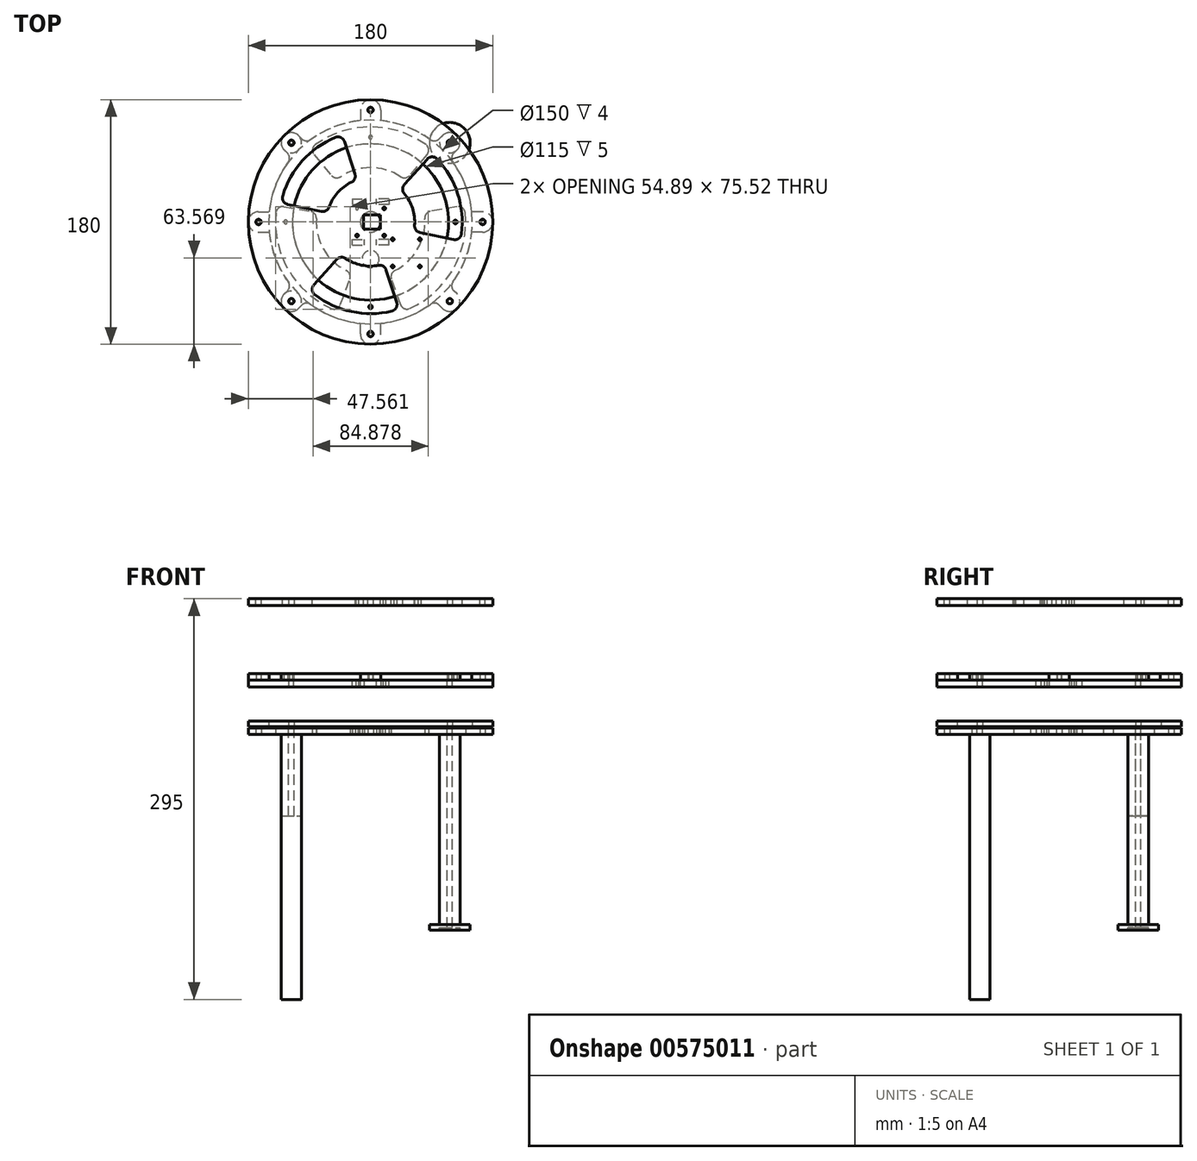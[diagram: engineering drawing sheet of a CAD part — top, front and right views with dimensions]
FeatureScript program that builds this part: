
annotation { "Feature Type Name" : "Feature", "Feature Type Description" : "" }
export const myFeature = defineFeature(function(context is Context, id is Id, definition is map)
    precondition{}
    {
        {
            var Q0;
            Q0=qCreatedBy(makeId("Top.planeOp"),FACE);
            var sketch = newSketch(context, id + "F0", { "sketchPlane" : qUnion([Q0])});
            skCircle(sketch, "E0", {"center": v(0, 0) * mm, "radius": 90 * mm});
            skCircle(sketch, "E1", {"center": v(0, 0) * mm, "radius": 75 * mm});
            skLineSegment(sketch, "E2", {"start": v(-75, 0) * mm, "end": v(-90, 0) * mm, "construction": true});
            skCircle(sketch, "E3", {"center": v(0, 0) * mm, "radius": 82.5 * mm, "construction": true});
            skPoint(sketch, "E4", {"position": v(-82.5, 0) * mm});
            skLineSegment(sketch, "E5", {"start": v(0, 0) * mm, "end": v(-58.34, 58.34) * mm, "construction": true});
            skCircle(sketch, "E6", {"center": v(-58.34, 58.34) * mm, "radius": 2 * mm});
            skCircle(sketch, "E7.MirrorC", {"center": v(58.34, 58.34) * mm, "radius": 2 * mm});
            skCircle(sketch, "E8.MirrorC", {"center": v(-58.34, -58.34) * mm, "radius": 2 * mm});
            skCircle(sketch, "E9.MirrorC", {"center": v(58.34, -58.34) * mm, "radius": 2 * mm});
            skSolve(sketch);
        }
        {
            var Q0;
            Q0 = qSketchRegion(id + "F0", true);
            extrude(context, id + "F1", {"entities" : qUnion([Q0]), "depth" : 4 * mm, "offsetDistance" : 25 * mm});
        }
        {
            var Q0;
            Q0=makeQuery(id+"F1.opExtrude","CAP_FACE",FACE,{"disambiguationData":[OSD([sQuery(id+"F0.wireOp",EDGE,"E0"),sQuery(id+"F0.wireOp",EDGE,"E1"),sQuery(id+"F0.wireOp",EDGE,"E6"),sQuery(id+"F0.wireOp",EDGE,"E7.MirrorC"),sQuery(id+"F0.wireOp",EDGE,"E8.MirrorC"),sQuery(id+"F0.wireOp",EDGE,"E9.MirrorC")])],"isStart":true});
            cPlane(context, id + "F2", {"entities" : qUnion([Q0]), "cplaneType" : CPlaneType.OFFSET, "offset" : 1 * mm, "width" : 150 * mm, "height" : 150 * mm});
        }
        {
            var Q0;
            Q0=qCreatedBy(id+"F2.planeOp",FACE);
            var sketch = newSketch(context, id + "F3", { "sketchPlane" : qUnion([Q0])});
            skCircle(sketch, "E10.0", {"center": v(0, 0) * mm, "radius": 90 * mm});
            skCircle(sketch, "E11.0", {"center": v(-58.34, 58.34) * mm, "radius": 2 * mm});
            skCircle(sketch, "E12.0", {"center": v(58.34, 58.34) * mm, "radius": 2 * mm});
            skCircle(sketch, "E13.0", {"center": v(58.34, -58.34) * mm, "radius": 2 * mm});
            skCircle(sketch, "E14.0", {"center": v(-58.34, -58.34) * mm, "radius": 2 * mm});
            skCircle(sketch, "E15", {"center": v(0, 0) * mm, "radius": 7.55 * mm});
            skSolve(sketch);
        }
        {
            var Q0;
            Q0 = qSketchRegion(id + "F3", true);
            extrude(context, id + "F4", {"entities" : qUnion([Q0]), "depth" : 5 * mm, "offsetDistance" : 25 * mm});
        }
        {
            var Q0;
            Q0=makeQuery(id+"F4.opExtrude","CAP_FACE",FACE,{"disambiguationData":[OSD([sQuery(id+"F3.wireOp",EDGE,"E10.0"),sQuery(id+"F3.wireOp",EDGE,"E11.0"),sQuery(id+"F3.wireOp",EDGE,"E12.0"),sQuery(id+"F3.wireOp",EDGE,"E13.0"),sQuery(id+"F3.wireOp",EDGE,"E14.0"),sQuery(id+"F3.wireOp",EDGE,"E15")])],"isStart":true});
            var sketch = newSketch(context, id + "F5", { "sketchPlane" : qUnion([Q0])});
            skLineSegment(sketch, "E16.bottom", {"start": v(-10, 10) * mm, "end": v(10, 10) * mm, "construction": true});
            skLineSegment(sketch, "E16.top", {"start": v(-10, -10) * mm, "end": v(10, -10) * mm, "construction": true});
            skLineSegment(sketch, "E16.left", {"start": v(-10, 10) * mm, "end": v(-10, -10) * mm, "construction": true});
            skLineSegment(sketch, "E16.right", {"start": v(10, 10) * mm, "end": v(10, -10) * mm, "construction": true});
            skPoint(sketch, "E16.middle", {"position": v(0, 0) * mm});
            skCircle(sketch, "E17", {"center": v(-10, 10) * mm, "radius": 1 * mm});
            skCircle(sketch, "E18.MirrorC", {"center": v(10, 10) * mm, "radius": 1 * mm});
            skCircle(sketch, "E19.MirrorC", {"center": v(-10, -10) * mm, "radius": 1 * mm});
            skCircle(sketch, "E20.MirrorC", {"center": v(10, -10) * mm, "radius": 1 * mm});
            skSolve(sketch);
        }
        {
            var Q0;
            Q0 = qSketchRegion(id + "F5", true);
            extrude(context, id + "F6", {"entities" : qUnion([Q0]), "operationType" : NewBodyOperationType.REMOVE, "endBound" : BoundingType.UP_TO_NEXT, "oppositeDirection" : true, "depth" : 25 * mm, "offsetDistance" : 25 * mm});
        }
        {
            var Q0;
            Q0=makeQuery(id+"F4.opExtrude","CAP_FACE",FACE,{"disambiguationData":[OSD([sQuery(id+"F3.wireOp",EDGE,"E10.0"),sQuery(id+"F3.wireOp",EDGE,"E11.0"),sQuery(id+"F3.wireOp",EDGE,"E12.0"),sQuery(id+"F3.wireOp",EDGE,"E13.0"),sQuery(id+"F3.wireOp",EDGE,"E14.0"),sQuery(id+"F3.wireOp",EDGE,"E15")])],"isStart":false});
            var sketch = newSketch(context, id + "F7", { "sketchPlane" : qUnion([Q0])});
            skPoint(sketch, "E21.center", {"position": v(0, 0) * mm});
            skCircle(sketch, "E22", {"center": v(-58.34, 58.34) * mm, "radius": 7.5 * mm});
            skSolve(sketch);
        }
        {
            var Q0;
            Q0 = qSketchRegion(id + "F7", true);
            extrude(context, id + "F8", {"entities" : qUnion([Q0]), "depth" : 195 * mm, "offsetDistance" : 25 * mm});
        }
        {
            var Q0;
            Q0=makeQuery(id+"F4.opExtrude","CAP_FACE",FACE,{"disambiguationData":[OSD([sQuery(id+"F3.wireOp",EDGE,"E10.0"),sQuery(id+"F3.wireOp",EDGE,"E11.0"),sQuery(id+"F3.wireOp",EDGE,"E12.0"),sQuery(id+"F3.wireOp",EDGE,"E13.0"),sQuery(id+"F3.wireOp",EDGE,"E14.0"),sQuery(id+"F3.wireOp",EDGE,"E15")])],"isStart":false});
            cPlane(context, id + "F9", {"entities" : qUnion([Q0]), "cplaneType" : CPlaneType.OFFSET, "offset" : 20 * mm, "oppositeDirection" : true, "width" : 150 * mm, "height" : 150 * mm});
        }
        {
            var Q0;
            Q0=makeQuery(id+"F4.opExtrude","SWEPT_BODY",BODY,{"disambiguationData":[OSD([sQuery(id+"F3.wireOp",EDGE,"E10.0"),sQuery(id+"F3.wireOp",EDGE,"E11.0"),sQuery(id+"F3.wireOp",EDGE,"E12.0"),sQuery(id+"F3.wireOp",EDGE,"E13.0"),sQuery(id+"F3.wireOp",EDGE,"E14.0"),sQuery(id+"F3.wireOp",EDGE,"E15")])]});
            var Q1;
            Q1=qCreatedBy(id+"F9.planeOp",FACE);
            mirror(context, id + "F10", {"entities" : qUnion([Q0]), "mirrorPlane" : qUnion([Q1])});
        }
        {
            var Q0;
            Q0=makeQuery(id+"F10.opPattern","COPY",FACE,{"derivedFrom":makeQuery(id+"F4.opExtrude","CAP_FACE",FACE,{"disambiguationData":[OSD([sQuery(id+"F3.wireOp",EDGE,"E10.0"),sQuery(id+"F3.wireOp",EDGE,"E11.0"),sQuery(id+"F3.wireOp",EDGE,"E12.0"),sQuery(id+"F3.wireOp",EDGE,"E13.0"),sQuery(id+"F3.wireOp",EDGE,"E14.0"),sQuery(id+"F3.wireOp",EDGE,"E15")])],"isStart":false}),"instanceName":"1"});
            var sketch = newSketch(context, id + "F11", { "sketchPlane" : qUnion([Q0])});
            skLineSegment(sketch, "E23.bottom", {"start": v(13, -13) * mm, "end": v(-13, -13) * mm, "construction": true});
            skLineSegment(sketch, "E23.top", {"start": v(13, -17) * mm, "end": v(-13, -17) * mm, "construction": true});
            skLineSegment(sketch, "E23.left", {"start": v(13, -13) * mm, "end": v(13, -17) * mm, "construction": true});
            skLineSegment(sketch, "E23.right", {"start": v(-13, -13) * mm, "end": v(-13, -17) * mm, "construction": true});
            skPoint(sketch, "E23.middle", {"position": v(0, -15) * mm});
            skLineSegment(sketch, "E24", {"start": v(5, -13) * mm, "end": v(5, -17) * mm, "construction": true});
            skLineSegment(sketch, "E25.MirrorCS", {"start": v(-5, -13) * mm, "end": v(-5, -17) * mm, "construction": true});
            skLineSegment(sketch, "E26", {"start": v(5, -13) * mm, "end": v(13, -17) * mm, "construction": true});
            skPoint(sketch, "E27", {"position": v(9, -15) * mm});
            skLineSegment(sketch, "E28.bottom", {"start": v(4.5, -13) * mm, "end": v(13.5, -13) * mm});
            skLineSegment(sketch, "E28.top", {"start": v(4.5, -17) * mm, "end": v(13.5, -17) * mm});
            skLineSegment(sketch, "E28.left", {"start": v(4.5, -13) * mm, "end": v(4.5, -17) * mm});
            skLineSegment(sketch, "E28.right", {"start": v(13.5, -13) * mm, "end": v(13.5, -17) * mm});
            skLineSegment(sketch, "E29.MirrorCS", {"start": v(-4.5, -13) * mm, "end": v(-4.5, -17) * mm});
            skLineSegment(sketch, "E30.MirrorCS", {"start": v(-4.5, -13) * mm, "end": v(-13.5, -13) * mm});
            skLineSegment(sketch, "E31.MirrorCS", {"start": v(-13.5, -13) * mm, "end": v(-13.5, -17) * mm});
            skLineSegment(sketch, "E32.MirrorCS", {"start": v(-4.5, -17) * mm, "end": v(-13.5, -17) * mm});
            skLineSegment(sketch, "E33.MirrorCS", {"start": v(-13.5, 13) * mm, "end": v(-13.5, 17) * mm});
            skLineSegment(sketch, "E34.MirrorCS", {"start": v(-4.5, 13) * mm, "end": v(-13.5, 13) * mm});
            skLineSegment(sketch, "E35.MirrorCS", {"start": v(-4.5, 13) * mm, "end": v(-4.5, 17) * mm});
            skLineSegment(sketch, "E36.MirrorCS", {"start": v(-4.5, 17) * mm, "end": v(-13.5, 17) * mm});
            skLineSegment(sketch, "E37.MirrorCS", {"start": v(4.5, 13) * mm, "end": v(4.5, 17) * mm});
            skLineSegment(sketch, "E38.MirrorCS", {"start": v(4.5, 13) * mm, "end": v(13.5, 13) * mm});
            skLineSegment(sketch, "E39.MirrorCS", {"start": v(13.5, 13) * mm, "end": v(13.5, 17) * mm});
            skLineSegment(sketch, "E40.MirrorCS", {"start": v(4.5, 17) * mm, "end": v(13.5, 17) * mm});
            skSolve(sketch);
        }
        {
            var Q0;
            Q0 = qSketchRegion(id + "F11", true);
            extrude(context, id + "F12", {"entities" : qUnion([Q0]), "operationType" : NewBodyOperationType.REMOVE, "endBound" : BoundingType.UP_TO_NEXT, "oppositeDirection" : true, "depth" : 25 * mm, "offsetDistance" : 25 * mm});
        }
        {
            var Q0;
            Q0=makeQuery(id+"F10.opPattern","COPY",FACE,{"derivedFrom":makeQuery(id+"F4.opExtrude","CAP_FACE",FACE,{"disambiguationData":[OSD([sQuery(id+"F3.wireOp",EDGE,"E10.0"),sQuery(id+"F3.wireOp",EDGE,"E11.0"),sQuery(id+"F3.wireOp",EDGE,"E12.0"),sQuery(id+"F3.wireOp",EDGE,"E13.0"),sQuery(id+"F3.wireOp",EDGE,"E14.0"),sQuery(id+"F3.wireOp",EDGE,"E15")])],"isStart":false}),"instanceName":"1"});
            var sketch = newSketch(context, id + "F13", { "sketchPlane" : qUnion([Q0])});
            skCircle(sketch, "E41", {"center": v(-58.34, 58.34) * mm, "radius": 1.85 * mm});
            skCircle(sketch, "E42.0", {"center": v(-58.34, 58.34) * mm, "radius": 2 * mm});
            skCircle(sketch, "E43.1.0", {"center": v(-58.34, -58.34) * mm, "radius": 1.85 * mm});
            skCircle(sketch, "E43.1.1", {"center": v(-58.34, -58.34) * mm, "radius": 2 * mm});
            skCircle(sketch, "E43.2.0", {"center": v(58.34, -58.34) * mm, "radius": 1.85 * mm});
            skCircle(sketch, "E43.2.1", {"center": v(58.34, -58.34) * mm, "radius": 2 * mm});
            skCircle(sketch, "E43.3.0", {"center": v(58.34, 58.34) * mm, "radius": 1.85 * mm});
            skCircle(sketch, "E43.3.1", {"center": v(58.34, 58.34) * mm, "radius": 2 * mm});
            skPoint(sketch, "E43.center", {"position": v(0, 0) * mm});
            skSolve(sketch);
        }
        {
            var Q0;
            Q0 = qSketchRegion(id + "F13", true);
            var Q1;
            Q1=makeQuery(id+"F10.opPattern","COPY",FACE,{"derivedFrom":makeQuery(id+"F4.opExtrude","CAP_FACE",FACE,{"disambiguationData":[OSD([sQuery(id+"F3.wireOp",EDGE,"E10.0"),sQuery(id+"F3.wireOp",EDGE,"E11.0"),sQuery(id+"F3.wireOp",EDGE,"E12.0"),sQuery(id+"F3.wireOp",EDGE,"E13.0"),sQuery(id+"F3.wireOp",EDGE,"E14.0"),sQuery(id+"F3.wireOp",EDGE,"E15")])],"isStart":true}),"instanceName":"1"});
            extrude(context, id + "F14", {"entities" : qUnion([Q0]), "operationType" : NewBodyOperationType.ADD, "endBound" : BoundingType.UP_TO_SURFACE, "oppositeDirection" : true, "depth" : 25 * mm, "endBoundEntityFace" : qUnion([Q1]), "offsetDistance" : 25 * mm});
        }
        {
            var Q0;
            Q0=makeQuery(id+"F14.boolean.opBoolean","MERGE",FACE,{"derivedFrom":[makeQuery(id+"F10.opPattern","COPY",FACE,{"derivedFrom":makeQuery(id+"F4.opExtrude","CAP_FACE",FACE,{"disambiguationData":[OSD([sQuery(id+"F3.wireOp",EDGE,"E10.0"),sQuery(id+"F3.wireOp",EDGE,"E11.0"),sQuery(id+"F3.wireOp",EDGE,"E12.0"),sQuery(id+"F3.wireOp",EDGE,"E13.0"),sQuery(id+"F3.wireOp",EDGE,"E14.0"),sQuery(id+"F3.wireOp",EDGE,"E15")])],"isStart":false}),"instanceName":"1"}),makeQuery(id+"F14.opExtrude","CAP_FACE",FACE,{"disambiguationData":[OSD([sQuery(id+"F13.wireOp",EDGE,"E41"),sQuery(id+"F13.wireOp",EDGE,"E42.0")])],"isStart":true}),makeQuery(id+"F14.opExtrude","CAP_FACE",FACE,{"disambiguationData":[OSD([sQuery(id+"F13.wireOp",EDGE,"E43.1.0"),sQuery(id+"F13.wireOp",EDGE,"E43.1.1")])],"isStart":true}),makeQuery(id+"F14.opExtrude","CAP_FACE",FACE,{"disambiguationData":[OSD([sQuery(id+"F13.wireOp",EDGE,"E43.2.0"),sQuery(id+"F13.wireOp",EDGE,"E43.2.1")])],"isStart":true}),makeQuery(id+"F14.opExtrude","CAP_FACE",FACE,{"disambiguationData":[OSD([sQuery(id+"F13.wireOp",EDGE,"E43.3.0"),sQuery(id+"F13.wireOp",EDGE,"E43.3.1")])],"isStart":true})]});
            var sketch = newSketch(context, id + "F15", { "sketchPlane" : qUnion([Q0])});
            skCircle(sketch, "E44.0", {"center": v(-58.34, 58.34) * mm, "radius": 1.85 * mm});
            skCircle(sketch, "E45.0", {"center": v(-58.34, -58.34) * mm, "radius": 1.85 * mm});
            skCircle(sketch, "E46.0", {"center": v(58.34, -58.34) * mm, "radius": 1.85 * mm});
            skCircle(sketch, "E47.0", {"center": v(58.34, 58.34) * mm, "radius": 1.85 * mm});
            skArc(sketch, "E48", {"start": v(63.64, 53.03) * mm, "mid": v(63.64, 63.64) * mm, "end": v(53.03, 63.64) * mm});
            skCircle(sketch, "E49", {"center": v(0, 0) * mm, "radius": 57.5 * mm});
            skArc(sketch, "E50", {"start": v(47.46, 58.07) * mm, "mid": v(0, 75) * mm, "end": v(-47.46, 58.07) * mm});
            skLineSegment(sketch, "E51", {"start": v(58.34, 58.34) * mm, "end": v(63.64, 53.03) * mm, "construction": true});
            skLineSegment(sketch, "E52", {"start": v(58.34, 58.34) * mm, "end": v(0, 0) * mm, "construction": true});
            skLineSegment(sketch, "E53", {"start": v(63.64, 53.03) * mm, "end": v(58.07, 47.46) * mm});
            skLineSegment(sketch, "E54.MirrorCS", {"start": v(53.03, 63.64) * mm, "end": v(47.46, 58.07) * mm});
            skLineSegment(sketch, "E55.MirrorCS", {"start": v(-53.03, 63.64) * mm, "end": v(-47.46, 58.07) * mm});
            skArc(sketch, "E56.MirrorCS", {"start": v(-63.64, 53.03) * mm, "mid": v(-63.64, 63.64) * mm, "end": v(-53.03, 63.64) * mm});
            skLineSegment(sketch, "E57.MirrorCS", {"start": v(-63.64, 53.03) * mm, "end": v(-58.07, 47.46) * mm});
            skLineSegment(sketch, "E58.MirrorCS", {"start": v(58.34, -58.34) * mm, "end": v(59.64, -57.03) * mm, "construction": true});
            skLineSegment(sketch, "E59.MirrorCS", {"start": v(-63.64, -53.03) * mm, "end": v(-58.07, -47.46) * mm});
            skLineSegment(sketch, "E60.MirrorCS", {"start": v(63.64, -53.03) * mm, "end": v(58.07, -47.46) * mm});
            skArc(sketch, "E61.MirrorCS", {"start": v(63.64, -53.03) * mm, "mid": v(63.64, -63.64) * mm, "end": v(53.03, -63.64) * mm});
            skLineSegment(sketch, "E62.MirrorCS", {"start": v(53.03, -63.64) * mm, "end": v(47.46, -58.07) * mm});
            skLineSegment(sketch, "E63.MirrorCS", {"start": v(-53.03, -63.64) * mm, "end": v(-47.46, -58.07) * mm});
            skArc(sketch, "E64.MirrorCS", {"start": v(-63.64, -53.03) * mm, "mid": v(-63.64, -63.64) * mm, "end": v(-53.03, -63.64) * mm});
            skArc(sketch, "E65.trimOffspring", {"start": v(-58.07, 47.46) * mm, "mid": v(-75, 0) * mm, "end": v(-58.07, -47.46) * mm});
            skArc(sketch, "E66.trimOffspring", {"start": v(-47.46, -58.07) * mm, "mid": v(0, -75) * mm, "end": v(47.46, -58.07) * mm});
            skArc(sketch, "E67.trimOffspring", {"start": v(58.07, -47.46) * mm, "mid": v(75, 0) * mm, "end": v(58.07, 47.46) * mm});
            skCircle(sketch, "E68", {"center": v(0, 62.5) * mm, "radius": 1.35 * mm});
            skCircle(sketch, "E69.1.0", {"center": v(-62.5, 0) * mm, "radius": 1.35 * mm});
            skCircle(sketch, "E69.2.0", {"center": v(0, -62.5) * mm, "radius": 1.35 * mm});
            skCircle(sketch, "E70.1.3.0", {"center": v(62.5, 0) * mm, "radius": 1.35 * mm});
            skLineSegment(sketch, "E71.1.0", {"start": v(-7.5, 82.5) * mm, "end": v(-7.5, 74.62) * mm});
            skArc(sketch, "E71.1.1", {"start": v(7.5, 82.5) * mm, "mid": v(0, 90) * mm, "end": v(-7.5, 82.5) * mm});
            skLineSegment(sketch, "E71.1.2", {"start": v(7.5, 82.5) * mm, "end": v(7.5, 74.62) * mm});
            skCircle(sketch, "E71.1.3", {"center": v(0, 82.5) * mm, "radius": 1.85 * mm});
            skArc(sketch, "E71.2.1", {"start": v(-53.03, 63.64) * mm, "mid": v(-63.64, 63.64) * mm, "end": v(-63.64, 53.03) * mm});
            skLineSegment(sketch, "E71.3.0", {"start": v(-82.5, -7.5) * mm, "end": v(-74.62, -7.5) * mm});
            skArc(sketch, "E71.3.1", {"start": v(-82.5, 7.5) * mm, "mid": v(-90, 0) * mm, "end": v(-82.5, -7.5) * mm});
            skLineSegment(sketch, "E71.3.2", {"start": v(-82.5, 7.5) * mm, "end": v(-74.62, 7.5) * mm});
            skCircle(sketch, "E71.3.3", {"center": v(-82.5, 0) * mm, "radius": 1.85 * mm});
            skLineSegment(sketch, "E71.5.0", {"start": v(7.5, -82.5) * mm, "end": v(7.5, -74.62) * mm});
            skArc(sketch, "E71.5.1", {"start": v(-7.5, -82.5) * mm, "mid": v(0, -90) * mm, "end": v(7.5, -82.5) * mm});
            skLineSegment(sketch, "E71.5.2", {"start": v(-7.5, -82.5) * mm, "end": v(-7.5, -74.62) * mm});
            skCircle(sketch, "E71.5.3", {"center": v(0, -82.5) * mm, "radius": 1.85 * mm});
            skArc(sketch, "E71.6.1", {"start": v(53.03, -63.64) * mm, "mid": v(63.64, -63.64) * mm, "end": v(63.64, -53.03) * mm});
            skLineSegment(sketch, "E71.7.0", {"start": v(82.5, 7.5) * mm, "end": v(74.62, 7.5) * mm});
            skArc(sketch, "E71.7.1", {"start": v(82.5, -7.5) * mm, "mid": v(90, 0) * mm, "end": v(82.5, 7.5) * mm});
            skLineSegment(sketch, "E71.7.2", {"start": v(82.5, -7.5) * mm, "end": v(74.62, -7.5) * mm});
            skCircle(sketch, "E71.7.3", {"center": v(82.5, 0) * mm, "radius": 1.85 * mm});
            skSolve(sketch);
        }
        {
            var Q0;
            Q0 = qSketchRegion(id + "F15", true);
            extrude(context, id + "F16", {"entities" : qUnion([Q0]), "depth" : 5 * mm, "offsetDistance" : 25 * mm});
        }
        {
            var Q0;
            Q0=makeQuery(id+"F16.opExtrude","SWEPT_EDGE",EDGE,{"disambiguationData":[OSD([sQuery(id+"F15.wireOp",EDGE,"E50"),sQuery(id+"F15.wireOp",EDGE,"E55.MirrorCS")])]});
            var Q1;
            Q1=makeQuery(id+"F16.opExtrude","SWEPT_EDGE",EDGE,{"disambiguationData":[OSD([sQuery(id+"F15.wireOp",EDGE,"E50"),sQuery(id+"F15.wireOp",EDGE,"E54.MirrorCS")])]});
            var Q2;
            Q2=makeQuery(id+"F16.opExtrude","SWEPT_EDGE",EDGE,{"disambiguationData":[OSD([sQuery(id+"F15.wireOp",EDGE,"E53"),sQuery(id+"F15.wireOp",EDGE,"E67.trimOffspring")])]});
            var Q3;
            Q3=makeQuery(id+"F16.opExtrude","SWEPT_EDGE",EDGE,{"disambiguationData":[OSD([sQuery(id+"F15.wireOp",EDGE,"E60.MirrorCS"),sQuery(id+"F15.wireOp",EDGE,"E67.trimOffspring")])]});
            var Q4;
            Q4=makeQuery(id+"F16.opExtrude","SWEPT_EDGE",EDGE,{"disambiguationData":[OSD([sQuery(id+"F15.wireOp",EDGE,"E62.MirrorCS"),sQuery(id+"F15.wireOp",EDGE,"E66.trimOffspring")])]});
            var Q5;
            Q5=makeQuery(id+"F16.opExtrude","SWEPT_EDGE",EDGE,{"disambiguationData":[OSD([sQuery(id+"F15.wireOp",EDGE,"E63.MirrorCS"),sQuery(id+"F15.wireOp",EDGE,"E66.trimOffspring")])]});
            var Q6;
            Q6=makeQuery(id+"F16.opExtrude","SWEPT_EDGE",EDGE,{"disambiguationData":[OSD([sQuery(id+"F15.wireOp",EDGE,"E59.MirrorCS"),sQuery(id+"F15.wireOp",EDGE,"E65.trimOffspring")])]});
            var Q7;
            Q7=makeQuery(id+"F16.opExtrude","SWEPT_EDGE",EDGE,{"disambiguationData":[OSD([sQuery(id+"F15.wireOp",EDGE,"E57.MirrorCS"),sQuery(id+"F15.wireOp",EDGE,"E65.trimOffspring")])]});
            fillet(context, id + "F17", {"entities" : qUnion([Q0, Q1, Q2, Q3, Q4, Q5, Q6, Q7]), "radius" : 5 * mm, "tangentPropagation" : true, "allowEdgeOverflow" : false});
        }
        {
            var Q0;
            Q0=makeQuery(id+"F4.opExtrude","CAP_FACE",FACE,{"disambiguationData":[OSD([sQuery(id+"F3.wireOp",EDGE,"E10.0"),sQuery(id+"F3.wireOp",EDGE,"E11.0"),sQuery(id+"F3.wireOp",EDGE,"E12.0"),sQuery(id+"F3.wireOp",EDGE,"E13.0"),sQuery(id+"F3.wireOp",EDGE,"E14.0"),sQuery(id+"F3.wireOp",EDGE,"E15")])],"isStart":false});
            var sketch = newSketch(context, id + "F18", { "sketchPlane" : qUnion([Q0])});
            skCircle(sketch, "E72", {"center": v(58.34, -58.34) * mm, "radius": 7.5 * mm});
            skCircle(sketch, "E73.0", {"center": v(58.34, -58.34) * mm, "radius": 2 * mm});
            skSolve(sketch);
        }
        {
            var Q0;
            Q0 = qSketchRegion(id + "F18", true);
            extrude(context, id + "F19", {"entities" : qUnion([Q0]), "depth" : 140 * mm, "offsetDistance" : 25 * mm});
        }
        {
            var Q0;
            Q0=makeQuery(id+"F19.opExtrude","CAP_FACE",FACE,{"disambiguationData":[OSD([sQuery(id+"F18.wireOp",EDGE,"E72"),sQuery(id+"F18.wireOp",EDGE,"E73.0")])],"isStart":false});
            var sketch = newSketch(context, id + "F20", { "sketchPlane" : qUnion([Q0])});
            skCircle(sketch, "E74.0", {"center": v(58.34, -58.34) * mm, "radius": 7.5 * mm});
            skCircle(sketch, "E75.0", {"center": v(58.34, -58.34) * mm, "radius": 2 * mm});
            skCircle(sketch, "E76", {"center": v(58.34, -58.34) * mm, "radius": 15 * mm});
            skSolve(sketch);
        }
        {
            var Q0;
            Q0=makeQuery(id+"F20.imprint","IMPRINT",FACE,{"disambiguationData":[TD([[makeQuery(id+"F20.imprint","IMPRINT",EDGE,{"derivedFrom":sQuery(id+"F20.wireOp",EDGE,"E74.0")}),-1.0]])]});
            extrude(context, id + "F21", {"entities" : qUnion([Q0]), "depth" : 4 * mm, "offsetDistance" : 25 * mm});
        }
        {
            var Q0;
            Q0=makeQuery(id+"F19.opExtrude","CAP_FACE",FACE,{"disambiguationData":[OSD([sQuery(id+"F18.wireOp",EDGE,"E72"),sQuery(id+"F18.wireOp",EDGE,"E73.0")])],"isStart":false});
            extrude(context, id + "F22", {"entities" : qUnion([Q0]), "operationType" : NewBodyOperationType.ADD, "depth" : 2 * mm, "offsetDistance" : 25 * mm});
        }
        {
            var Q0;
            Q0=makeQuery(id+"F14.boolean.opBoolean","MERGE",FACE,{"derivedFrom":[makeQuery(id+"F10.opPattern","COPY",FACE,{"derivedFrom":makeQuery(id+"F4.opExtrude","CAP_FACE",FACE,{"disambiguationData":[OSD([sQuery(id+"F3.wireOp",EDGE,"E10.0"),sQuery(id+"F3.wireOp",EDGE,"E11.0"),sQuery(id+"F3.wireOp",EDGE,"E12.0"),sQuery(id+"F3.wireOp",EDGE,"E13.0"),sQuery(id+"F3.wireOp",EDGE,"E14.0"),sQuery(id+"F3.wireOp",EDGE,"E15")])],"isStart":false}),"instanceName":"1"}),makeQuery(id+"F14.opExtrude","CAP_FACE",FACE,{"disambiguationData":[OSD([sQuery(id+"F13.wireOp",EDGE,"E41"),sQuery(id+"F13.wireOp",EDGE,"E42.0")])],"isStart":true}),makeQuery(id+"F14.opExtrude","CAP_FACE",FACE,{"disambiguationData":[OSD([sQuery(id+"F13.wireOp",EDGE,"E43.1.0"),sQuery(id+"F13.wireOp",EDGE,"E43.1.1")])],"isStart":true}),makeQuery(id+"F14.opExtrude","CAP_FACE",FACE,{"disambiguationData":[OSD([sQuery(id+"F13.wireOp",EDGE,"E43.2.0"),sQuery(id+"F13.wireOp",EDGE,"E43.2.1")])],"isStart":true}),makeQuery(id+"F14.opExtrude","CAP_FACE",FACE,{"disambiguationData":[OSD([sQuery(id+"F13.wireOp",EDGE,"E43.3.0"),sQuery(id+"F13.wireOp",EDGE,"E43.3.1")])],"isStart":true})]});
            cPlane(context, id + "F23", {"entities" : qUnion([Q0]), "cplaneType" : CPlaneType.OFFSET, "offset" : 10 * mm, "width" : 150 * mm, "height" : 150 * mm});
        }
        {
            var Q0;
            Q0=makeQuery(id+"F4.opExtrude","SWEPT_BODY",BODY,{"disambiguationData":[OSD([sQuery(id+"F3.wireOp",EDGE,"E10.0"),sQuery(id+"F3.wireOp",EDGE,"E11.0"),sQuery(id+"F3.wireOp",EDGE,"E12.0"),sQuery(id+"F3.wireOp",EDGE,"E13.0"),sQuery(id+"F3.wireOp",EDGE,"E14.0"),sQuery(id+"F3.wireOp",EDGE,"E15")])]});
            var Q1;
            Q1=qCreatedBy(id+"F23.planeOp",FACE);
            mirror(context, id + "F24", {"entities" : qUnion([Q0]), "mirrorPlane" : qUnion([Q1])});
        }
        {
            var Q0;
            Q0=makeQuery(id+"F24.opPattern","COPY",FACE,{"derivedFrom":makeQuery(id+"F4.opExtrude","CAP_FACE",FACE,{"disambiguationData":[OSD([sQuery(id+"F3.wireOp",EDGE,"E10.0"),sQuery(id+"F3.wireOp",EDGE,"E11.0"),sQuery(id+"F3.wireOp",EDGE,"E12.0"),sQuery(id+"F3.wireOp",EDGE,"E13.0"),sQuery(id+"F3.wireOp",EDGE,"E14.0"),sQuery(id+"F3.wireOp",EDGE,"E15")])],"isStart":false}),"instanceName":"1"});
            var sketch = newSketch(context, id + "F25", { "sketchPlane" : qUnion([Q0])});
            skCircle(sketch, "E77.0", {"center": v(-10, -10) * mm, "radius": 1 * mm});
            skCircle(sketch, "E78.0", {"center": v(-10, 10) * mm, "radius": 1 * mm});
            skCircle(sketch, "E79.0", {"center": v(10, 10) * mm, "radius": 1 * mm});
            skCircle(sketch, "E80.0", {"center": v(-58.34, 58.34) * mm, "radius": 2 * mm});
            skCircle(sketch, "E81.1.0", {"center": v(-82.5, 0) * mm, "radius": 2 * mm});
            skCircle(sketch, "E81.2.0", {"center": v(-58.34, -58.34) * mm, "radius": 2 * mm});
            skCircle(sketch, "E82.1.3.0", {"center": v(0, -82.5) * mm, "radius": 2 * mm});
            skCircle(sketch, "E82.1.4.0", {"center": v(58.34, -58.34) * mm, "radius": 2 * mm});
            skCircle(sketch, "E82.1.5.0", {"center": v(82.5, 0) * mm, "radius": 2 * mm});
            skCircle(sketch, "E82.1.6.0", {"center": v(58.34, 58.34) * mm, "radius": 2 * mm});
            skCircle(sketch, "E82.1.7.0", {"center": v(0, 82.5) * mm, "radius": 2 * mm});
            skLineSegment(sketch, "E83.bottom", {"start": v(-5.25, 5.25) * mm, "end": v(7.25, 5.25) * mm});
            skLineSegment(sketch, "E83.top", {"start": v(-5.25, -5.25) * mm, "end": v(7.25, -5.25) * mm});
            skLineSegment(sketch, "E83.left", {"start": v(-5.25, 5.25) * mm, "end": v(-5.25, -5.25) * mm});
            skLineSegment(sketch, "E83.right", {"start": v(7.25, 5.25) * mm, "end": v(7.25, -5.25) * mm});
            skPoint(sketch, "E83.middle", {"position": v(1, 0) * mm});
            skLineSegment(sketch, "E84.bottom", {"start": v(16.3, -12.75) * mm, "end": v(36.3, -12.75) * mm, "construction": true});
            skLineSegment(sketch, "E84.top", {"start": v(16.3, -32.75) * mm, "end": v(36.3, -32.75) * mm, "construction": true});
            skLineSegment(sketch, "E84.left", {"start": v(16.3, -12.75) * mm, "end": v(16.3, -32.75) * mm, "construction": true});
            skLineSegment(sketch, "E84.right", {"start": v(36.3, -12.75) * mm, "end": v(36.3, -32.75) * mm, "construction": true});
            skPoint(sketch, "E84.middle", {"position": v(26.3, -22.75) * mm});
            skCircle(sketch, "E85.0", {"center": v(10, -10) * mm, "radius": 1 * mm, "construction": true});
            skCircle(sketch, "E86", {"center": v(16.3, -12.75) * mm, "radius": 1 * mm});
            skCircle(sketch, "E87.1.0", {"center": v(16.3, -32.75) * mm, "radius": 1 * mm});
            skCircle(sketch, "E87.2.0", {"center": v(36.3, -32.75) * mm, "radius": 1 * mm});
            skCircle(sketch, "E88.1.3.0", {"center": v(36.3, -12.75) * mm, "radius": 1 * mm});
            skSolve(sketch);
        }
        {
            var Q0;
            {var subQ0=sQuery(id+"F25.wireOp",EDGE,"QSQis5DJ-ndRP-tXz9-sWgT-VjHo9YrmBDyp.right");var subQ1=sQuery(id+"F25.wireOp",EDGE,"15366a01-08b8-4944-8cce-0e4f2887150d.0");var subQ2=makeQuery(id+"F25.imprint","INTERSECT",VERTEX,{"disambiguationData":[OD(0.0)],"derivedFrom":[subQ1,subQ0]});Q0=makeQuery(id+"F25.imprint","IMPRINT",FACE,{"disambiguationData":[TD([[makeQuery(id+"F25.imprint","IMPRINT",EDGE,{"disambiguationData":[TD([[subQ2,1.0]])],"derivedFrom":subQ1}),-1.0]])]});}
            var Q1;
            Q1=makeQuery(id+"F25.imprint","IMPRINT",FACE,{"disambiguationData":[TD([[makeQuery(id+"F25.imprint","IMPRINT",EDGE,{"derivedFrom":sQuery(id+"F25.wireOp",EDGE,"E78.0")}),1.0]])]});
            var Q2;
            Q2=makeQuery(id+"F25.imprint","IMPRINT",FACE,{"disambiguationData":[TD([[makeQuery(id+"F25.imprint","IMPRINT",EDGE,{"derivedFrom":sQuery(id+"F25.wireOp",EDGE,"E79.0")}),-1.0]])]});
            var Q3;
            Q3=makeQuery(id+"F25.imprint","IMPRINT",FACE,{"disambiguationData":[TD([[makeQuery(id+"F25.imprint","IMPRINT",EDGE,{"derivedFrom":sQuery(id+"F25.wireOp",EDGE,"950ba534-4a06-4b06-9c65-52ff77a1f382.0")}),1.0]])]});
            var Q4;
            Q4=makeQuery(id+"F25.imprint","IMPRINT",FACE,{"disambiguationData":[TD([[makeQuery(id+"F25.imprint","IMPRINT",EDGE,{"derivedFrom":sQuery(id+"F25.wireOp",EDGE,"E77.0")}),-1.0]])]});
            var Q5;
            {var subQ0=sQuery(id+"F25.wireOp",EDGE,"QSQis5DJ-ndRP-tXz9-sWgT-VjHo9YrmBDyp.left");var subQ1=sQuery(id+"F25.wireOp",EDGE,"15366a01-08b8-4944-8cce-0e4f2887150d.0");var subQ2=makeQuery(id+"F25.imprint","INTERSECT",VERTEX,{"disambiguationData":[OD(0.0)],"derivedFrom":[subQ1,subQ0]});Q5=makeQuery(id+"F25.imprint","IMPRINT",FACE,{"disambiguationData":[TD([[makeQuery(id+"F25.imprint","IMPRINT",EDGE,{"disambiguationData":[TD([[subQ2,-1.0]])],"derivedFrom":subQ1}),-1.0]])]});}
            var Q6;
            {var subQ0=sQuery(id+"F25.wireOp",EDGE,"QSQis5DJ-ndRP-tXz9-sWgT-VjHo9YrmBDyp.bottom");var subQ1=sQuery(id+"F25.wireOp",EDGE,"15366a01-08b8-4944-8cce-0e4f2887150d.0");var subQ2=makeQuery(id+"F25.imprint","INTERSECT",VERTEX,{"disambiguationData":[OD(0.0)],"derivedFrom":[subQ1,subQ0]});Q6=makeQuery(id+"F25.imprint","IMPRINT",FACE,{"disambiguationData":[TD([[makeQuery(id+"F25.imprint","IMPRINT",EDGE,{"disambiguationData":[TD([[subQ2,-1.0]])],"derivedFrom":subQ1}),-1.0]])]});}
            var Q7;
            {var subQ0=sQuery(id+"F25.wireOp",EDGE,"QSQis5DJ-ndRP-tXz9-sWgT-VjHo9YrmBDyp.top");var subQ1=sQuery(id+"F25.wireOp",EDGE,"15366a01-08b8-4944-8cce-0e4f2887150d.0");var subQ2=makeQuery(id+"F25.imprint","INTERSECT",VERTEX,{"disambiguationData":[OD(0.0)],"derivedFrom":[subQ1,subQ0]});Q7=makeQuery(id+"F25.imprint","IMPRINT",FACE,{"disambiguationData":[TD([[makeQuery(id+"F25.imprint","IMPRINT",EDGE,{"disambiguationData":[TD([[subQ2,-1.0]])],"derivedFrom":subQ1}),-1.0]])]});}
            var Q8;
            {var subQ0=sQuery(id+"F25.wireOp",EDGE,"E83.left");Q8=makeQuery(id+"F25.imprint","IMPRINT",FACE,{"disambiguationData":[TD([[makeQuery(id+"F25.imprint","IMPRINT",EDGE,{"derivedFrom":subQ0}),-1.0]])]});}
            var Q9;
            {var subQ0=sQuery(id+"F25.wireOp",EDGE,"E83.right");var subQ1=makeQuery(id+"F24.opPattern","COPY",EDGE,{"derivedFrom":makeQuery(id+"F4.opExtrude","CAP_EDGE",EDGE,{"disambiguationData":[OSD([sQuery(id+"F3.wireOp",EDGE,"E15")])],"isStart":false}),"instanceName":"1"});var subQ2=makeQuery(id+"F25.imprint","INTERSECT",VERTEX,{"disambiguationData":[OD(0.0)],"derivedFrom":[subQ1,subQ0]});Q9=makeQuery(id+"F25.imprint","IMPRINT",FACE,{"disambiguationData":[TD([[makeQuery(id+"F25.imprint","IMPRINT",EDGE,{"disambiguationData":[TD([[subQ2,-1.0]])],"derivedFrom":subQ0}),1.0]])]});}
            var Q10;
            {var subQ3=sQuery(id+"F25.wireOp",EDGE,"X5iIHsC0-m7Zg-54nE-1Jfu-dFlnVcUJdtpu");var subQ8=sQuery(id+"F25.wireOp",EDGE,"a78230fa-ddc7-4092-8a09-10e84057542a0.MirrorCS");var subQ9=makeQuery(id+"F25.imprint","INTERSECT",VERTEX,{"derivedFrom":[subQ3,subQ8]});Q10=makeQuery(id+"F25.imprint","IMPRINT",FACE,{"disambiguationData":[TD([[makeQuery(id+"F25.imprint","IMPRINT",EDGE,{"disambiguationData":[TD([[subQ9,1.0]])],"derivedFrom":subQ3}),1.0]])]});}
            var Q11;
            Q11=makeQuery(id+"F25.imprint","IMPRINT",FACE,{"disambiguationData":[TD([[makeQuery(id+"F25.imprint","IMPRINT",EDGE,{"derivedFrom":makeQuery(id+"F24.opPattern","COPY",EDGE,{"derivedFrom":makeQuery(id+"F6.boolean.opBoolean","COPY",EDGE,{"derivedFrom":makeQuery(id+"F6.opExtrude","TWEAK_EDGE",EDGE,{"derivedFrom":[makeQuery(id+"F4.opExtrude","CAP_FACE",FACE,{"disambiguationData":[OSD([sQuery(id+"F3.wireOp",EDGE,"E10.0"),sQuery(id+"F3.wireOp",EDGE,"E11.0"),sQuery(id+"F3.wireOp",EDGE,"E12.0"),sQuery(id+"F3.wireOp",EDGE,"E13.0"),sQuery(id+"F3.wireOp",EDGE,"E14.0"),sQuery(id+"F3.wireOp",EDGE,"E15")])],"isStart":false}),makeQuery(id+"F5.imprint","IMPRINT",EDGE,{"derivedFrom":sQuery(id+"F5.wireOp",EDGE,"E20.MirrorC")})]})}),"instanceName":"1"})}),1.0]])]});
            extrude(context, id + "F26", {"entities" : qUnion([Q0, Q1, Q2, Q3, Q4, Q5, Q6, Q7, Q8, Q9, Q10, Q11]), "operationType" : NewBodyOperationType.ADD, "oppositeDirection" : true, "depth" : 5 * mm, "offsetDistance" : 25 * mm});
        }
        {
            var Q0;
            {var subQ5=sQuery(id+"F25.wireOp",EDGE,"656fdb2e-e72c-4114-8cef-4688475ef528.filletArc");Q0=makeQuery(id+"F25.imprint","IMPRINT",FACE,{"disambiguationData":[TD([[makeQuery(id+"F25.imprint","IMPRINT",EDGE,{"derivedFrom":subQ5}),1.0]])]});}
            var Q1;
            {var subQ5=sQuery(id+"F25.wireOp",EDGE,"dae69112-de24-48df-9be6-64b79decc6ef.filletArc");Q1=makeQuery(id+"F25.imprint","IMPRINT",FACE,{"disambiguationData":[TD([[makeQuery(id+"F25.imprint","IMPRINT",EDGE,{"derivedFrom":subQ5}),1.0]])]});}
            var Q2;
            {var subQ5=sQuery(id+"F25.wireOp",EDGE,"470e9d0d-4a14-41c7-af53-fb42cd5c9400.filletArc");Q2=makeQuery(id+"F25.imprint","IMPRINT",FACE,{"disambiguationData":[TD([[makeQuery(id+"F25.imprint","IMPRINT",EDGE,{"derivedFrom":subQ5}),1.0]])]});}
            var Q3;
            {var subQ5=sQuery(id+"F25.wireOp",EDGE,"ee6f9c0c-4a7c-40b4-91d3-26762448eaf5.filletArc");Q3=makeQuery(id+"F25.imprint","IMPRINT",FACE,{"disambiguationData":[TD([[makeQuery(id+"F25.imprint","IMPRINT",EDGE,{"derivedFrom":subQ5}),1.0]])]});}
            var Q4;
            Q4=makeQuery(id+"F25.imprint","IMPRINT",FACE,{"disambiguationData":[TD([[makeQuery(id+"F25.imprint","IMPRINT",EDGE,{"derivedFrom":sQuery(id+"F25.wireOp",EDGE,"X5iIHsC0-m7Zg-54nE-1Jfu-dFlnVcUJdtpu")}),1.0]])]});
            var Q5;
            Q5=makeQuery(id+"F25.imprint","IMPRINT",FACE,{"disambiguationData":[TD([[makeQuery(id+"F25.imprint","IMPRINT",EDGE,{"derivedFrom":sQuery(id+"F25.wireOp",EDGE,"QmYIbrE2-BVum-i9cv-bLCY-xA6qm9N7vCon")}),1.0]])]});
            var Q6;
            Q6=makeQuery(id+"F25.imprint","IMPRINT",FACE,{"disambiguationData":[TD([[makeQuery(id+"F25.imprint","IMPRINT",EDGE,{"derivedFrom":sQuery(id+"F25.wireOp",EDGE,"eadecacf-8e49-4b1c-866c-a8928ed26be7.1.3.0")}),1.0]])]});
            var Q7;
            Q7=makeQuery(id+"F25.imprint","IMPRINT",FACE,{"disambiguationData":[TD([[makeQuery(id+"F25.imprint","IMPRINT",EDGE,{"derivedFrom":sQuery(id+"F25.wireOp",EDGE,"7a315e59-80f9-47be-ab7b-8afd31b71271.2.0")}),1.0]])]});
            var Q8;
            Q8=makeQuery(id+"F25.imprint","IMPRINT",FACE,{"disambiguationData":[TD([[makeQuery(id+"F25.imprint","IMPRINT",EDGE,{"derivedFrom":sQuery(id+"F25.wireOp",EDGE,"7a315e59-80f9-47be-ab7b-8afd31b71271.1.0")}),1.0]])]});
            var Q9;
            {var subQ0=sQuery(id+"F25.wireOp",EDGE,"QSQis5DJ-ndRP-tXz9-sWgT-VjHo9YrmBDyp.bottom");var subQ1=sQuery(id+"F25.wireOp",EDGE,"15366a01-08b8-4944-8cce-0e4f2887150d.0");var subQ2=makeQuery(id+"F25.imprint","INTERSECT",VERTEX,{"disambiguationData":[OD(1.0)],"derivedFrom":[subQ1,subQ0]});Q9=makeQuery(id+"F25.imprint","IMPRINT",FACE,{"disambiguationData":[TD([[makeQuery(id+"F25.imprint","IMPRINT",EDGE,{"disambiguationData":[TD([[subQ2,-1.0]])],"derivedFrom":subQ1}),1.0]])]});}
            var Q10;
            {var subQ0=sQuery(id+"F25.wireOp",EDGE,"QSQis5DJ-ndRP-tXz9-sWgT-VjHo9YrmBDyp.top");var subQ1=sQuery(id+"F25.wireOp",EDGE,"15366a01-08b8-4944-8cce-0e4f2887150d.0");var subQ2=makeQuery(id+"F25.imprint","INTERSECT",VERTEX,{"disambiguationData":[OD(0.0)],"derivedFrom":[subQ1,subQ0]});Q10=makeQuery(id+"F25.imprint","IMPRINT",FACE,{"disambiguationData":[TD([[makeQuery(id+"F25.imprint","IMPRINT",EDGE,{"disambiguationData":[TD([[subQ2,1.0]])],"derivedFrom":subQ1}),1.0]])]});}
            var Q11;
            {var subQ0=sQuery(id+"F25.wireOp",EDGE,"QSQis5DJ-ndRP-tXz9-sWgT-VjHo9YrmBDyp.top");var subQ1=sQuery(id+"F25.wireOp",EDGE,"15366a01-08b8-4944-8cce-0e4f2887150d.0");var subQ2=makeQuery(id+"F25.imprint","INTERSECT",VERTEX,{"disambiguationData":[OD(1.0)],"derivedFrom":[subQ1,subQ0]});Q11=makeQuery(id+"F25.imprint","IMPRINT",FACE,{"disambiguationData":[TD([[makeQuery(id+"F25.imprint","IMPRINT",EDGE,{"disambiguationData":[TD([[subQ2,-1.0]])],"derivedFrom":subQ1}),1.0]])]});}
            var Q12;
            {var subQ0=sQuery(id+"F25.wireOp",EDGE,"QSQis5DJ-ndRP-tXz9-sWgT-VjHo9YrmBDyp.left");var subQ1=sQuery(id+"F25.wireOp",EDGE,"15366a01-08b8-4944-8cce-0e4f2887150d.0");var subQ2=makeQuery(id+"F25.imprint","INTERSECT",VERTEX,{"disambiguationData":[OD(1.0)],"derivedFrom":[subQ1,subQ0]});Q12=makeQuery(id+"F25.imprint","IMPRINT",FACE,{"disambiguationData":[TD([[makeQuery(id+"F25.imprint","IMPRINT",EDGE,{"disambiguationData":[TD([[subQ2,-1.0]])],"derivedFrom":subQ1}),1.0]])]});}
            var Q13;
            Q13=makeQuery(id+"F25.imprint","IMPRINT",FACE,{"disambiguationData":[TD([[makeQuery(id+"F25.imprint","IMPRINT",EDGE,{"derivedFrom":sQuery(id+"F25.wireOp",EDGE,"E82.1.3.0")}),1.0]])]});
            var Q14;
            Q14=makeQuery(id+"F25.imprint","IMPRINT",FACE,{"disambiguationData":[TD([[makeQuery(id+"F25.imprint","IMPRINT",EDGE,{"derivedFrom":sQuery(id+"F25.wireOp",EDGE,"E82.1.5.0")}),1.0]])]});
            var Q15;
            Q15=makeQuery(id+"F25.imprint","IMPRINT",FACE,{"disambiguationData":[TD([[makeQuery(id+"F25.imprint","IMPRINT",EDGE,{"derivedFrom":sQuery(id+"F25.wireOp",EDGE,"E82.1.7.0")}),1.0]])]});
            var Q16;
            Q16=makeQuery(id+"F25.imprint","IMPRINT",FACE,{"disambiguationData":[TD([[makeQuery(id+"F25.imprint","IMPRINT",EDGE,{"derivedFrom":sQuery(id+"F25.wireOp",EDGE,"E81.1.0")}),1.0]])]});
            var Q17;
            {var subQ0=sQuery(id+"F25.wireOp",EDGE,"E83.right");var subQ1=sQuery(id+"F25.wireOp",EDGE,"E83.bottom");var subQ2=makeQuery(id+"F25.imprint","INTERSECT",VERTEX,{"derivedFrom":[subQ1,subQ0]});Q17=makeQuery(id+"F25.imprint","IMPRINT",FACE,{"disambiguationData":[TD([[makeQuery(id+"F25.imprint","IMPRINT",EDGE,{"disambiguationData":[TD([[subQ2,1.0]])],"derivedFrom":subQ1}),-1.0]])]});}
            var Q18;
            {var subQ0=sQuery(id+"F25.wireOp",EDGE,"E83.right");var subQ1=sQuery(id+"F25.wireOp",EDGE,"E83.top");var subQ2=makeQuery(id+"F25.imprint","INTERSECT",VERTEX,{"derivedFrom":[subQ1,subQ0]});Q18=makeQuery(id+"F25.imprint","IMPRINT",FACE,{"disambiguationData":[TD([[makeQuery(id+"F25.imprint","IMPRINT",EDGE,{"disambiguationData":[TD([[subQ2,1.0]])],"derivedFrom":subQ1}),1.0]])]});}
            var Q19;
            Q19=makeQuery(id+"F25.imprint","IMPRINT",FACE,{"disambiguationData":[TD([[makeQuery(id+"F25.imprint","IMPRINT",EDGE,{"derivedFrom":sQuery(id+"F25.wireOp",EDGE,"XyLoIunc-2Nd5-WO0a-HkcV-batRIsL5vsgj.bottom")}),-1.0]])]});
            var Q20;
            Q20=makeQuery(id+"F25.imprint","IMPRINT",FACE,{"disambiguationData":[TD([[makeQuery(id+"F25.imprint","IMPRINT",EDGE,{"derivedFrom":sQuery(id+"F25.wireOp",EDGE,"950ba534-4a06-4b06-9c65-52ff77a1f382.0")}),-1.0]])]});
            var Q21;
            Q21=makeQuery(id+"F25.imprint","IMPRINT",FACE,{"disambiguationData":[TD([[makeQuery(id+"F25.imprint","IMPRINT",EDGE,{"derivedFrom":sQuery(id+"F25.wireOp",EDGE,"950ba534-4a06-4b06-9c65-52ff77a1f382.0")}),1.0]])]});
            var Q22;
            Q22=makeQuery(id+"F25.imprint","IMPRINT",FACE,{"disambiguationData":[TD([[makeQuery(id+"F25.imprint","IMPRINT",EDGE,{"derivedFrom":sQuery(id+"F25.wireOp",EDGE,"E86")}),1.0]])]});
            var Q23;
            Q23=makeQuery(id+"F25.imprint","IMPRINT",FACE,{"disambiguationData":[TD([[makeQuery(id+"F25.imprint","IMPRINT",EDGE,{"derivedFrom":sQuery(id+"F25.wireOp",EDGE,"E88.1.3.0")}),1.0]])]});
            var Q24;
            Q24=makeQuery(id+"F25.imprint","IMPRINT",FACE,{"disambiguationData":[TD([[makeQuery(id+"F25.imprint","IMPRINT",EDGE,{"derivedFrom":sQuery(id+"F25.wireOp",EDGE,"E87.2.0")}),1.0]])]});
            var Q25;
            Q25=makeQuery(id+"F25.imprint","IMPRINT",FACE,{"disambiguationData":[TD([[makeQuery(id+"F25.imprint","IMPRINT",EDGE,{"derivedFrom":sQuery(id+"F25.wireOp",EDGE,"E87.1.0")}),1.0]])]});
            extrude(context, id + "F27", {"entities" : qUnion([Q0, Q1, Q2, Q3, Q4, Q5, Q6, Q7, Q8, Q9, Q10, Q11, Q12, Q13, Q14, Q15, Q16, Q17, Q18, Q19, Q20, Q21, Q22, Q23, Q24, Q25]), "operationType" : NewBodyOperationType.REMOVE, "oppositeDirection" : true, "depth" : 5 * mm, "offsetDistance" : 25 * mm});
        }
        {
            var Q0;
            Q0=makeQuery(id+"F4.opExtrude","CAP_FACE",FACE,{"disambiguationData":[OSD([sQuery(id+"F3.wireOp",EDGE,"E10.0"),sQuery(id+"F3.wireOp",EDGE,"E11.0"),sQuery(id+"F3.wireOp",EDGE,"E12.0"),sQuery(id+"F3.wireOp",EDGE,"E13.0"),sQuery(id+"F3.wireOp",EDGE,"E14.0"),sQuery(id+"F3.wireOp",EDGE,"E15")])],"isStart":false});
            var sketch = newSketch(context, id + "F28", { "sketchPlane" : qUnion([Q0])});
            skCircle(sketch, "E89.0", {"center": v(-58.34, -58.34) * mm, "radius": 2 * mm});
            skCircle(sketch, "E90", {"center": v(-58.34, -58.34) * mm, "radius": 7.5 * mm});
            skSolve(sketch);
        }
        {
            var Q0;
            Q0 = qSketchRegion(id + "F28", true);
            extrude(context, id + "F29", {"entities" : qUnion([Q0]), "depth" : 60 * mm, "offsetDistance" : 25 * mm});
        }
        {
            var Q0;
            Q0=makeQuery(id+"F4.opExtrude","CAP_FACE",FACE,{"disambiguationData":[OSD([sQuery(id+"F3.wireOp",EDGE,"E10.0"),sQuery(id+"F3.wireOp",EDGE,"E11.0"),sQuery(id+"F3.wireOp",EDGE,"E12.0"),sQuery(id+"F3.wireOp",EDGE,"E13.0"),sQuery(id+"F3.wireOp",EDGE,"E14.0"),sQuery(id+"F3.wireOp",EDGE,"E15")])],"isStart":false});
            var sketch = newSketch(context, id + "F30", { "sketchPlane" : qUnion([Q0])});
            skArc(sketch, "E91", {"start": v(-28.93, 63.74) * mm, "mid": v(-60.62, 35) * mm, "end": v(-69.67, -6.82) * mm});
            skArc(sketch, "E92", {"start": v(-17.77, 35.83) * mm, "mid": v(-34.64, 20) * mm, "end": v(-39.92, -2.53) * mm});
            skLineSegment(sketch, "E93", {"start": v(0, 0) * mm, "end": v(0, 70) * mm, "construction": true});
            skPoint(sketch, "E94", {"position": v(0, 40) * mm});
            skPoint(sketch, "E95", {"position": v(0, 90) * mm});
            skLineSegment(sketch, "E96", {"start": v(-22.17, 60.9) * mm, "end": v(-15.3, 42.02) * mm});
            skLineSegment(sketch, "E97.MirrorCS", {"start": v(22.17, 60.9) * mm, "end": v(15.3, 42.02) * mm});
            skLineSegment(sketch, "E98.1.0", {"start": v(-41.66, -49.65) * mm, "end": v(-28.75, -34.26) * mm});
            skLineSegment(sketch, "E98.1.1", {"start": v(-63.82, -11.25) * mm, "end": v(-44.04, -7.77) * mm});
            skLineSegment(sketch, "E98.2.0", {"start": v(63.82, -11.25) * mm, "end": v(44.04, -7.77) * mm});
            skLineSegment(sketch, "E98.2.1", {"start": v(41.66, -49.65) * mm, "end": v(28.75, -34.26) * mm});
            skArc(sketch, "E99.trimOffspring", {"start": v(69.67, -6.82) * mm, "mid": v(60.62, 35) * mm, "end": v(28.93, 63.74) * mm});
            skArc(sketch, "E100.trimOffspring", {"start": v(39.92, -2.53) * mm, "mid": v(34.64, 20) * mm, "end": v(17.77, 35.83) * mm});
            skArc(sketch, "E101.trimOffspring", {"start": v(-22.15, -33.3) * mm, "mid": v(0, -40) * mm, "end": v(22.15, -33.3) * mm});
            skArc(sketch, "E102.trimOffspring", {"start": v(-40.74, -56.93) * mm, "mid": v(0, -70) * mm, "end": v(40.74, -56.93) * mm});
            skPoint(sketch, "E103.visualSharp", {"position": v(-23.94, 65.78) * mm});
            skArc(sketch, "E103.filletArc", {"start": v(-22.17, 60.9) * mm, "mid": v(-24.93, 63.8) * mm, "end": v(-28.93, 63.74) * mm});
            skPoint(sketch, "E104.visualSharp", {"position": v(-13.68, 37.59) * mm});
            skArc(sketch, "E104.filletArc", {"start": v(-17.77, 35.83) * mm, "mid": v(-15.35, 38.46) * mm, "end": v(-15.3, 42.02) * mm});
            skPoint(sketch, "E105.visualSharp", {"position": v(13.68, 37.59) * mm});
            skArc(sketch, "E105.filletArc", {"start": v(15.3, 42.02) * mm, "mid": v(15.35, 38.46) * mm, "end": v(17.77, 35.83) * mm});
            skPoint(sketch, "E106.visualSharp", {"position": v(23.94, 65.78) * mm});
            skArc(sketch, "E106.filletArc", {"start": v(28.93, 63.74) * mm, "mid": v(24.93, 63.8) * mm, "end": v(22.17, 60.9) * mm});
            skPoint(sketch, "E107.visualSharp", {"position": v(68.94, -12.16) * mm});
            skArc(sketch, "E107.filletArc", {"start": v(63.82, -11.25) * mm, "mid": v(67.71, -10.31) * mm, "end": v(69.67, -6.82) * mm});
            skPoint(sketch, "E108.visualSharp", {"position": v(39.4, -6.95) * mm});
            skArc(sketch, "E108.filletArc", {"start": v(39.92, -2.53) * mm, "mid": v(40.98, -5.93) * mm, "end": v(44.04, -7.77) * mm});
            skPoint(sketch, "E109.visualSharp", {"position": v(-39.4, -6.95) * mm});
            skArc(sketch, "E109.filletArc", {"start": v(-44.04, -7.77) * mm, "mid": v(-40.98, -5.93) * mm, "end": v(-39.92, -2.53) * mm});
            skPoint(sketch, "E110.visualSharp", {"position": v(-68.94, -12.16) * mm});
            skArc(sketch, "E110.filletArc", {"start": v(-69.67, -6.82) * mm, "mid": v(-67.71, -10.31) * mm, "end": v(-63.82, -11.25) * mm});
            skPoint(sketch, "E111.visualSharp", {"position": v(-25.71, -30.64) * mm});
            skArc(sketch, "E111.filletArc", {"start": v(-22.15, -33.3) * mm, "mid": v(-25.63, -32.52) * mm, "end": v(-28.75, -34.26) * mm});
            skPoint(sketch, "E112.visualSharp", {"position": v(-45, -53.62) * mm});
            skArc(sketch, "E112.filletArc", {"start": v(-41.66, -49.65) * mm, "mid": v(-42.79, -53.49) * mm, "end": v(-40.74, -56.93) * mm});
            skPoint(sketch, "E113.visualSharp", {"position": v(25.71, -30.64) * mm});
            skArc(sketch, "E113.filletArc", {"start": v(28.75, -34.26) * mm, "mid": v(25.63, -32.52) * mm, "end": v(22.15, -33.3) * mm});
            skPoint(sketch, "E114.visualSharp", {"position": v(45, -53.62) * mm});
            skArc(sketch, "E114.filletArc", {"start": v(40.74, -56.93) * mm, "mid": v(42.79, -53.49) * mm, "end": v(41.66, -49.65) * mm});
            skCircle(sketch, "E115.0", {"center": v(58.34, 58.34) * mm, "radius": 2 * mm});
            skCircle(sketch, "E116.1.0", {"center": v(0, 82.5) * mm, "radius": 2 * mm});
            skCircle(sketch, "E116.2.0", {"center": v(-58.34, 58.34) * mm, "radius": 2 * mm});
            skCircle(sketch, "E117.1.3.0", {"center": v(-82.5, 0) * mm, "radius": 2 * mm});
            skCircle(sketch, "E117.1.4.0", {"center": v(-58.34, -58.34) * mm, "radius": 2 * mm});
            skCircle(sketch, "E117.1.5.0", {"center": v(0, -82.5) * mm, "radius": 2 * mm});
            skCircle(sketch, "E117.1.6.0", {"center": v(58.34, -58.34) * mm, "radius": 2 * mm});
            skCircle(sketch, "E117.1.7.0", {"center": v(82.5, 0) * mm, "radius": 2 * mm});
            skLineSegment(sketch, "E118.0", {"start": v(-13.5, 17) * mm, "end": v(-13.5, 13) * mm});
            skLineSegment(sketch, "E119.0", {"start": v(-13.5, 17) * mm, "end": v(-4.5, 17) * mm});
            skLineSegment(sketch, "E120.0", {"start": v(-4.5, 17) * mm, "end": v(-4.5, 13) * mm});
            skLineSegment(sketch, "E121.0", {"start": v(-13.5, 13) * mm, "end": v(-4.5, 13) * mm});
            skPoint(sketch, "E122.0", {"position": v(-13.5, -17) * mm});
            skLineSegment(sketch, "E123.0", {"start": v(-13.5, -17) * mm, "end": v(-13.5, -13) * mm});
            skLineSegment(sketch, "E124.0", {"start": v(-13.5, -13) * mm, "end": v(-4.5, -13) * mm});
            skLineSegment(sketch, "E125.0", {"start": v(-4.5, -17) * mm, "end": v(-4.5, -13) * mm});
            skLineSegment(sketch, "E126.0", {"start": v(-13.5, -17) * mm, "end": v(-4.5, -17) * mm});
            skLineSegment(sketch, "E127.0", {"start": v(13.5, -13) * mm, "end": v(4.5, -13) * mm});
            skLineSegment(sketch, "E128.0", {"start": v(13.5, -17) * mm, "end": v(4.5, -17) * mm});
            skLineSegment(sketch, "E129.0", {"start": v(13.5, -17) * mm, "end": v(13.5, -13) * mm});
            skLineSegment(sketch, "E130.0", {"start": v(4.5, 17) * mm, "end": v(4.5, 13) * mm});
            skLineSegment(sketch, "E131.0", {"start": v(13.5, 17) * mm, "end": v(4.5, 17) * mm});
            skLineSegment(sketch, "E132.0", {"start": v(13.5, 13) * mm, "end": v(4.5, 13) * mm});
            skLineSegment(sketch, "E133.0", {"start": v(13.5, 17) * mm, "end": v(13.5, 13) * mm});
            skCircle(sketch, "E134", {"center": v(0, 27.35) * mm, "radius": 6.25 * mm});
            skLineSegment(sketch, "E135", {"start": v(4.5, -13) * mm, "end": v(4.5, -17) * mm});
            skSolve(sketch);
        }
        {
            var Q0;
            Q0 = qSketchRegion(id + "F30", true);
            extrude(context, id + "F31", {"entities" : qUnion([Q0]), "operationType" : NewBodyOperationType.REMOVE, "oppositeDirection" : true, "depth" : 5 * mm, "offsetDistance" : 25 * mm});
        }
        {
            var Q0;
            {var subQ0=sQuery(id+"F3.wireOp",EDGE,"E15");Q0=makeQuery(id+"F26.boolean.opBoolean","MERGE",FACE,{"derivedFrom":[makeQuery(id+"F24.opPattern","COPY",FACE,{"derivedFrom":makeQuery(id+"F4.opExtrude","CAP_FACE",FACE,{"disambiguationData":[OSD([sQuery(id+"F3.wireOp",EDGE,"E10.0"),sQuery(id+"F3.wireOp",EDGE,"E11.0"),sQuery(id+"F3.wireOp",EDGE,"E12.0"),sQuery(id+"F3.wireOp",EDGE,"E13.0"),sQuery(id+"F3.wireOp",EDGE,"E14.0"),subQ0])],"isStart":false}),"instanceName":"1"}),makeQuery(id+"F26.opExtrude","CAP_FACE",FACE,{"disambiguationData":[OSD([sQuery(id+"F25.wireOp",EDGE,"E77.0")])],"isStart":true}),makeQuery(id+"F26.opExtrude","CAP_FACE",FACE,{"disambiguationData":[OSD([sQuery(id+"F25.wireOp",EDGE,"E78.0")])],"isStart":true}),makeQuery(id+"F26.opExtrude","CAP_FACE",FACE,{"disambiguationData":[OSD([sQuery(id+"F25.wireOp",EDGE,"E79.0")])],"isStart":true}),makeQuery(id+"F26.opExtrude","CAP_FACE",FACE,{"disambiguationData":[OSD([sQuery(id+"F25.wireOp",EDGE,"950ba534-4a06-4b06-9c65-52ff77a1f382.0")])],"isStart":true}),makeQuery(id+"F26.opExtrude","CAP_FACE",FACE,{"disambiguationData":[OSD([subQ0,sQuery(id+"F25.wireOp",EDGE,"E83.bottom"),sQuery(id+"F25.wireOp",EDGE,"E83.top"),sQuery(id+"F25.wireOp",EDGE,"E83.left")])],"isStart":true}),makeQuery(id+"F26.opExtrude","CAP_FACE",FACE,{"disambiguationData":[OSD([subQ0,sQuery(id+"F25.wireOp",EDGE,"E83.right")])],"isStart":true})]});}
            var sketch = newSketch(context, id + "F32", { "sketchPlane" : qUnion([Q0])});
            skArc(sketch, "E136", {"start": v(-41, -53.61) * mm, "mid": v(-14.03, -66.02) * mm, "end": v(15.66, -65.66) * mm});
            skArc(sketch, "E137", {"start": v(-18.33, -26.84) * mm, "mid": v(-6.76, -31.79) * mm, "end": v(5.83, -31.97) * mm});
            skLineSegment(sketch, "E138", {"start": v(0, 0) * mm, "end": v(0, 67.5) * mm, "construction": true});
            skPoint(sketch, "E139", {"position": v(0, 32.5) * mm});
            skLineSegment(sketch, "E140", {"start": v(-24.87, -27.62) * mm, "end": v(-41.69, -46.3) * mm});
            skLineSegment(sketch, "E141", {"start": v(-36.35, 7.73) * mm, "end": v(-60.94, 12.95) * mm});
            skLineSegment(sketch, "E142.MirrorCS", {"start": v(0, 0) * mm, "end": v(0, -67.5) * mm, "construction": true});
            skLineSegment(sketch, "E143.1.0", {"start": v(11.48, -35.35) * mm, "end": v(19.25, -59.25) * mm});
            skLineSegment(sketch, "E143.1.1", {"start": v(36.35, -7.73) * mm, "end": v(60.94, -12.95) * mm});
            skLineSegment(sketch, "E143.2.0", {"start": v(24.87, 27.62) * mm, "end": v(41.69, 46.3) * mm});
            skLineSegment(sketch, "E143.2.1", {"start": v(-11.48, 35.35) * mm, "end": v(-19.25, 59.25) * mm});
            skArc(sketch, "E144.trimOffspring", {"start": v(-25.93, 62.32) * mm, "mid": v(-50.16, 45.17) * mm, "end": v(-64.7, 19.27) * mm});
            skArc(sketch, "E145.trimOffspring", {"start": v(-14.07, 29.3) * mm, "mid": v(-24.15, 21.75) * mm, "end": v(-30.6, 10.94) * mm});
            skArc(sketch, "E146.trimOffspring", {"start": v(66.94, -8.7) * mm, "mid": v(64.2, 20.86) * mm, "end": v(49.03, 46.39) * mm});
            skArc(sketch, "E147.trimOffspring", {"start": v(32.4, -2.46) * mm, "mid": v(30.9, 10.04) * mm, "end": v(24.77, 21.04) * mm});
            skLineSegment(sketch, "E148", {"start": v(21.75, 24.15) * mm, "end": v(-10.04, 30.9) * mm, "construction": true});
            skLineSegment(sketch, "E149", {"start": v(0, 0) * mm, "end": v(5.85, 27.53) * mm, "construction": true});
            skPoint(sketch, "E150.visualSharp", {"position": v(45.17, 50.16) * mm});
            skArc(sketch, "E150.filletArc", {"start": v(49.03, 46.39) * mm, "mid": v(45.34, 47.95) * mm, "end": v(41.69, 46.3) * mm});
            skPoint(sketch, "E151.visualSharp", {"position": v(21.75, 24.15) * mm});
            skArc(sketch, "E151.filletArc", {"start": v(24.87, 27.62) * mm, "mid": v(23.58, 24.35) * mm, "end": v(24.77, 21.04) * mm});
            skPoint(sketch, "E152.visualSharp", {"position": v(31.79, -6.76) * mm});
            skArc(sketch, "E152.filletArc", {"start": v(32.4, -2.46) * mm, "mid": v(33.4, -5.83) * mm, "end": v(36.35, -7.73) * mm});
            skPoint(sketch, "E153.visualSharp", {"position": v(10.04, -30.9) * mm});
            skArc(sketch, "E153.filletArc", {"start": v(11.48, -35.35) * mm, "mid": v(9.3, -32.6) * mm, "end": v(5.83, -31.97) * mm});
            skPoint(sketch, "E154.visualSharp", {"position": v(-21.75, -24.15) * mm});
            skArc(sketch, "E154.filletArc", {"start": v(-18.33, -26.84) * mm, "mid": v(-21.75, -26) * mm, "end": v(-24.87, -27.62) * mm});
            skPoint(sketch, "E155.visualSharp", {"position": v(20.86, -64.2) * mm});
            skArc(sketch, "E155.filletArc", {"start": v(15.66, -65.66) * mm, "mid": v(18.86, -63.24) * mm, "end": v(19.25, -59.25) * mm});
            skPoint(sketch, "E156.visualSharp", {"position": v(-45.17, -50.16) * mm});
            skArc(sketch, "E156.filletArc", {"start": v(-41.69, -46.3) * mm, "mid": v(-42.95, -50.1) * mm, "end": v(-41, -53.61) * mm});
            skPoint(sketch, "E157.visualSharp", {"position": v(-31.79, 6.76) * mm});
            skArc(sketch, "E157.filletArc", {"start": v(-36.35, 7.73) * mm, "mid": v(-32.88, 8.25) * mm, "end": v(-30.6, 10.94) * mm});
            skPoint(sketch, "E158.visualSharp", {"position": v(-10.04, 30.9) * mm});
            skArc(sketch, "E158.filletArc", {"start": v(-14.07, 29.3) * mm, "mid": v(-11.64, 31.83) * mm, "end": v(-11.48, 35.35) * mm});
            skPoint(sketch, "E159.visualSharp", {"position": v(-20.86, 64.2) * mm});
            skArc(sketch, "E159.filletArc", {"start": v(-19.25, 59.25) * mm, "mid": v(-21.92, 62.25) * mm, "end": v(-25.93, 62.32) * mm});
            skPoint(sketch, "E160.visualSharp", {"position": v(-66.02, 14.03) * mm});
            skArc(sketch, "E160.filletArc", {"start": v(-64.7, 19.27) * mm, "mid": v(-64.2, 15.3) * mm, "end": v(-60.94, 12.95) * mm});
            skPoint(sketch, "E161.visualSharp", {"position": v(66.02, -14.03) * mm});
            skArc(sketch, "E161.filletArc", {"start": v(60.94, -12.95) * mm, "mid": v(64.87, -12.14) * mm, "end": v(66.94, -8.7) * mm});
            skPoint(sketch, "E162", {"position": v(30.9, 10.04) * mm});
            skSolve(sketch);
        }
        {
            var Q0;
            Q0=makeQuery(id+"F32.imprint","IMPRINT",FACE,{"disambiguationData":[TD([[makeQuery(id+"F32.imprint","IMPRINT",EDGE,{"derivedFrom":sQuery(id+"F32.wireOp",EDGE,"E136")}),1.0]])]});
            var Q1;
            Q1=makeQuery(id+"F32.imprint","IMPRINT",FACE,{"disambiguationData":[TD([[makeQuery(id+"F32.imprint","IMPRINT",EDGE,{"derivedFrom":sQuery(id+"F32.wireOp",EDGE,"E141")}),-1.0]])]});
            var Q2;
            Q2=makeQuery(id+"F32.imprint","IMPRINT",FACE,{"disambiguationData":[TD([[makeQuery(id+"F32.imprint","IMPRINT",EDGE,{"derivedFrom":sQuery(id+"F32.wireOp",EDGE,"E143.1.1")}),1.0]])]});
            extrude(context, id + "F33", {"entities" : qUnion([Q0, Q1, Q2]), "operationType" : NewBodyOperationType.REMOVE, "endBound" : BoundingType.UP_TO_NEXT, "oppositeDirection" : true, "depth" : 25 * mm, "offsetDistance" : 25 * mm});
        }
    });
